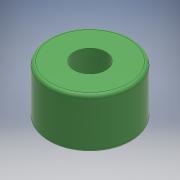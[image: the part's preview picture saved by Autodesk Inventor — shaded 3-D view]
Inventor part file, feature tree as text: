
AUTODESK INVENTOR PART (.ipt)
format: ipt  version: 2019 (Build 230136000, 136)  size: 123,392 bytes
history: native  units: mm
features: other x1, extrude x1, fillet x1, sketch x1
ambient origin geometry x8: Origin, YZ Plane, XZ Plane, XY Plane, X Axis, Y Axis, Z Axis, Center Point
bodies: Body1 (feature_tree)
feature tree (4):
  other  "Твердое тело1"
  extrude  "Выдавливание1"  Depth=25.0mm
  fillet  "Сопряжение1"  Radius=9.5mm
  sketch  "Эскиз1"
